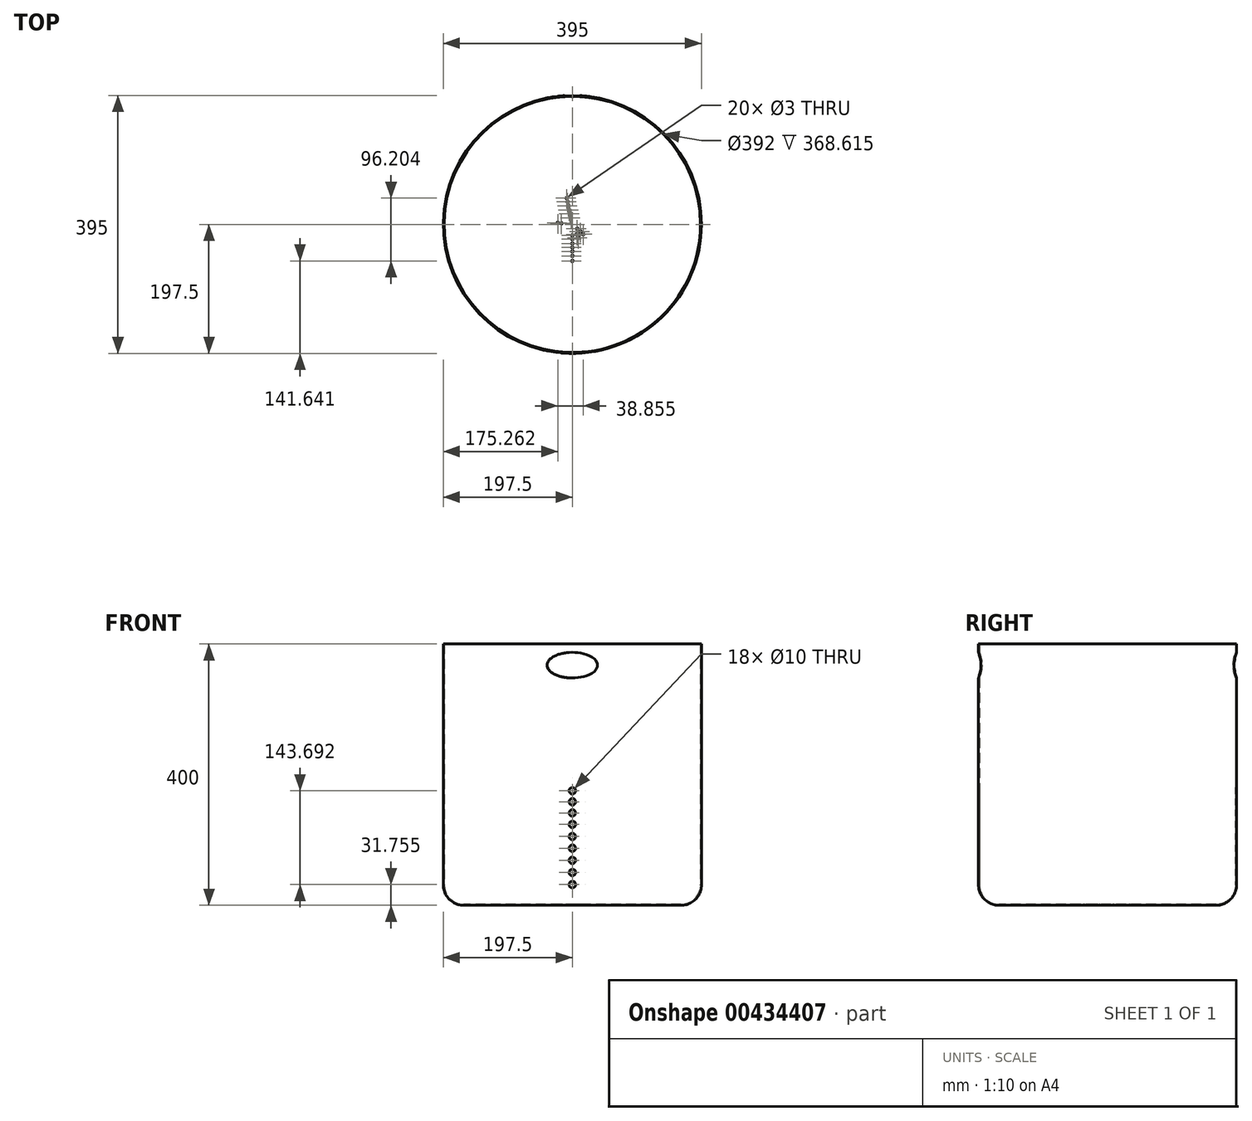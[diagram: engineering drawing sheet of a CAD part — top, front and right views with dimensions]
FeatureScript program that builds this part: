
annotation { "Feature Type Name" : "Feature", "Feature Type Description" : "" }
export const myFeature = defineFeature(function(context is Context, id is Id, definition is map)
    precondition{}
    {
        {
            var Q0;
            Q0=qCreatedBy(makeId("Top.planeOp"),FACE);
            var sketch = newSketch(context, id + "F0", { "sketchPlane" : qUnion([Q0])});
            skCircle(sketch, "E0", {"center": v(0, 0) * mm, "radius": 197.5 * mm});
            skSolve(sketch);
        }
        {
            var Q0;
            Q0 = qSketchRegion(id + "F0", true);
            extrude(context, id + "F1", {"entities" : qUnion([Q0]), "depth" : 400 * mm});
        }
        {
            var Q0;
            Q0=makeQuery(id+"F1.opExtrude","CAP_EDGE",EDGE,{"disambiguationData":[OSD([sQuery(id+"F0.wireOp",EDGE,"E0")])],"isStart":true});
            fillet(context, id + "F2", {"entities" : qUnion([Q0]), "radius" : 31.38 * mm, "tangentPropagation" : true, "allowEdgeOverflow" : false});
        }
        {
            var Q0;
            Q0=makeQuery(id+"F1.opExtrude","CAP_FACE",FACE,{"disambiguationData":[OSD([sQuery(id+"F0.wireOp",EDGE,"E0")])],"isStart":false});
            shell(context, id + "F3", {"entities" : qUnion([Q0]), "thickness" : 1.5 * mm});
        }
        {
            var Q0;
            Q0=makeQuery(id+"F1.opExtrude","CAP_FACE",FACE,{"disambiguationData":[OSD([sQuery(id+"F0.wireOp",EDGE,"E0")])],"isStart":true});
            var sketch = newSketch(context, id + "F4", { "sketchPlane" : qUnion([Q0])});
            skCircle(sketch, "E1", {"center": v(0, 3.82) * mm, "radius": 1.5 * mm});
            skCircle(sketch, "E2", {"center": v(0, 9.97) * mm, "radius": 1.5 * mm});
            skCircle(sketch, "E3", {"center": v(0, 16.8) * mm, "radius": 1.5 * mm});
            skCircle(sketch, "E4", {"center": v(0, 22.36) * mm, "radius": 1.5 * mm});
            skCircle(sketch, "E5", {"center": v(0, 29.28) * mm, "radius": 1.5 * mm});
            skCircle(sketch, "E6", {"center": v(0, 35.35) * mm, "radius": 1.5 * mm});
            skCircle(sketch, "E7", {"center": v(0, 41.25) * mm, "radius": 1.5 * mm});
            skCircle(sketch, "E8", {"center": v(0, 48.17) * mm, "radius": 1.5 * mm});
            skCircle(sketch, "E9", {"center": v(0, 55.86) * mm, "radius": 1.5 * mm});
            skCircle(sketch, "E10.1.0", {"center": v(-53.13, 17.26) * mm, "radius": 1.5 * mm});
            skCircle(sketch, "E10.1.1", {"center": v(-3.63, 1.18) * mm, "radius": 1.5 * mm});
            skCircle(sketch, "E10.1.2", {"center": v(-9.48, 3.08) * mm, "radius": 1.5 * mm});
            skCircle(sketch, "E10.1.3", {"center": v(-39.23, 12.75) * mm, "radius": 1.5 * mm});
            skCircle(sketch, "E10.1.4", {"center": v(-33.62, 10.92) * mm, "radius": 1.5 * mm});
            skCircle(sketch, "E10.1.5", {"center": v(-21.27, 6.9) * mm, "radius": 1.5 * mm});
            skCircle(sketch, "E10.1.6", {"center": v(-27.85, 9.05) * mm, "radius": 1.5 * mm});
            skCircle(sketch, "E10.1.7", {"center": v(-45.81, 14.88) * mm, "radius": 1.5 * mm});
            skCircle(sketch, "E10.1.8", {"center": v(-15.98, 5.2) * mm, "radius": 1.5 * mm});
            skCircle(sketch, "E10.2.0", {"center": v(-32.83, -45.2) * mm, "radius": 1.5 * mm});
            skCircle(sketch, "E10.2.1", {"center": v(-2.24, -3.09) * mm, "radius": 1.5 * mm});
            skCircle(sketch, "E10.2.2", {"center": v(-5.86, -8.07) * mm, "radius": 1.5 * mm});
            skCircle(sketch, "E10.2.3", {"center": v(-24.24, -33.37) * mm, "radius": 1.5 * mm});
            skCircle(sketch, "E10.2.4", {"center": v(-20.78, -28.6) * mm, "radius": 1.5 * mm});
            skCircle(sketch, "E10.2.5", {"center": v(-13.14, -18.1) * mm, "radius": 1.5 * mm});
            skCircle(sketch, "E10.2.6", {"center": v(-17.21, -23.7) * mm, "radius": 1.5 * mm});
            skCircle(sketch, "E10.2.7", {"center": v(-28.31, -38.97) * mm, "radius": 1.5 * mm});
            skCircle(sketch, "E10.2.8", {"center": v(-9.88, -13.6) * mm, "radius": 1.5 * mm});
            skCircle(sketch, "E10.3.0", {"center": v(32.83, -45.2) * mm, "radius": 1.5 * mm});
            skCircle(sketch, "E10.3.1", {"center": v(2.24, -3.09) * mm, "radius": 1.5 * mm});
            skCircle(sketch, "E10.3.2", {"center": v(5.86, -8.07) * mm, "radius": 1.5 * mm});
            skCircle(sketch, "E10.3.3", {"center": v(24.24, -33.37) * mm, "radius": 1.5 * mm});
            skCircle(sketch, "E10.3.4", {"center": v(20.78, -28.6) * mm, "radius": 1.5 * mm});
            skCircle(sketch, "E10.3.5", {"center": v(13.14, -18.1) * mm, "radius": 1.5 * mm});
            skCircle(sketch, "E10.3.6", {"center": v(17.21, -23.7) * mm, "radius": 1.5 * mm});
            skCircle(sketch, "E10.3.7", {"center": v(28.31, -38.97) * mm, "radius": 1.5 * mm});
            skCircle(sketch, "E10.3.8", {"center": v(9.88, -13.6) * mm, "radius": 1.5 * mm});
            skCircle(sketch, "E10.4.0", {"center": v(53.13, 17.26) * mm, "radius": 1.5 * mm});
            skCircle(sketch, "E10.4.1", {"center": v(3.63, 1.18) * mm, "radius": 1.5 * mm});
            skCircle(sketch, "E10.4.2", {"center": v(9.48, 3.08) * mm, "radius": 1.5 * mm});
            skCircle(sketch, "E10.4.3", {"center": v(39.23, 12.75) * mm, "radius": 1.5 * mm});
            skCircle(sketch, "E10.4.4", {"center": v(33.62, 10.92) * mm, "radius": 1.5 * mm});
            skCircle(sketch, "E10.4.5", {"center": v(21.27, 6.9) * mm, "radius": 1.5 * mm});
            skCircle(sketch, "E10.4.6", {"center": v(27.85, 9.05) * mm, "radius": 1.5 * mm});
            skCircle(sketch, "E10.4.7", {"center": v(45.81, 14.88) * mm, "radius": 1.5 * mm});
            skCircle(sketch, "E10.4.8", {"center": v(15.98, 5.2) * mm, "radius": 1.5 * mm});
            skPoint(sketch, "E10.center", {"position": v(0, 0) * mm});
            skCircle(sketch, "E11.1.0", {"center": v(-7.4, 6.67) * mm, "radius": 1.5 * mm});
            skCircle(sketch, "E11.1.1", {"center": v(-26.27, 23.65) * mm, "radius": 1.5 * mm});
            skCircle(sketch, "E11.1.2", {"center": v(-16.62, 14.96) * mm, "radius": 1.5 * mm});
            skCircle(sketch, "E11.1.3", {"center": v(-12.49, 11.25) * mm, "radius": 1.5 * mm});
            skCircle(sketch, "E11.1.4", {"center": v(-21.76, 19.6) * mm, "radius": 1.5 * mm});
            skCircle(sketch, "E11.1.5", {"center": v(6.84, 15.35) * mm, "radius": 1.5 * mm});
            skCircle(sketch, "E11.1.6", {"center": v(-35.8, 32.23) * mm, "radius": 1.5 * mm});
            skCircle(sketch, "E11.1.7", {"center": v(-30.65, 27.6) * mm, "radius": 1.5 * mm});
            skCircle(sketch, "E11.1.8", {"center": v(-41.51, 37.38) * mm, "radius": 1.5 * mm});
            skCircle(sketch, "E11.1.9", {"center": v(7.35, -34.58) * mm, "radius": 1.5 * mm});
            skCircle(sketch, "E11.1.10", {"center": v(6.09, -28.64) * mm, "radius": 1.5 * mm});
            skCircle(sketch, "E11.1.11", {"center": v(-8.63, -4.98) * mm, "radius": 1.5 * mm});
            skCircle(sketch, "E11.1.12", {"center": v(-14.55, -8.4) * mm, "radius": 1.5 * mm});
            skCircle(sketch, "E11.1.13", {"center": v(-19.36, -11.18) * mm, "radius": 1.5 * mm});
            skCircle(sketch, "E11.1.14", {"center": v(-25.36, -14.64) * mm, "radius": 1.5 * mm});
            skCircle(sketch, "E11.1.15", {"center": v(-30.61, -17.67) * mm, "radius": 1.5 * mm});
            skCircle(sketch, "E11.1.16", {"center": v(-35.72, -20.62) * mm, "radius": 1.5 * mm});
            skCircle(sketch, "E11.1.17", {"center": v(-41.71, -24.08) * mm, "radius": 1.5 * mm});
            skCircle(sketch, "E11.1.18", {"center": v(-48.38, -27.93) * mm, "radius": 1.5 * mm});
            skCircle(sketch, "E11.1.19", {"center": v(29.12, -3.06) * mm, "radius": 1.5 * mm});
            skCircle(sketch, "E11.1.20", {"center": v(35.16, -3.7) * mm, "radius": 1.5 * mm});
            skCircle(sketch, "E11.1.21", {"center": v(3.5, -16.44) * mm, "radius": 1.5 * mm});
            skCircle(sketch, "E11.1.22", {"center": v(4.65, -21.87) * mm, "radius": 1.5 * mm});
            skCircle(sketch, "E11.1.23", {"center": v(11.61, -54.64) * mm, "radius": 1.5 * mm});
            skCircle(sketch, "E11.1.24", {"center": v(8.58, -40.34) * mm, "radius": 1.5 * mm});
            skCircle(sketch, "E11.1.25", {"center": v(10.01, -47.12) * mm, "radius": 1.5 * mm});
            skCircle(sketch, "E11.1.26", {"center": v(22.24, -2.34) * mm, "radius": 1.5 * mm});
            skCircle(sketch, "E11.1.27", {"center": v(2.07, -9.75) * mm, "radius": 1.5 * mm});
            skCircle(sketch, "E11.1.28", {"center": v(55.55, -5.84) * mm, "radius": 1.5 * mm});
            skCircle(sketch, "E11.1.29", {"center": v(16.71, -1.76) * mm, "radius": 1.5 * mm});
            skCircle(sketch, "E11.1.30", {"center": v(41.02, -4.31) * mm, "radius": 1.5 * mm});
            skCircle(sketch, "E11.1.31", {"center": v(47.9, -5.03) * mm, "radius": 1.5 * mm});
            skCircle(sketch, "E11.1.32", {"center": v(9.1, 20.43) * mm, "radius": 1.5 * mm});
            skCircle(sketch, "E11.1.33", {"center": v(11.91, 26.75) * mm, "radius": 1.5 * mm});
            skCircle(sketch, "E11.1.34", {"center": v(14.38, 32.3) * mm, "radius": 1.5 * mm});
            skCircle(sketch, "E11.1.35", {"center": v(16.78, 37.68) * mm, "radius": 1.5 * mm});
            skCircle(sketch, "E11.1.36", {"center": v(19.6, 44) * mm, "radius": 1.5 * mm});
            skCircle(sketch, "E11.1.37", {"center": v(22.72, 51.03) * mm, "radius": 1.5 * mm});
            skCircle(sketch, "E11.2.0", {"center": v(-2.07, -9.75) * mm, "radius": 1.5 * mm});
            skCircle(sketch, "E11.2.1", {"center": v(-7.35, -34.58) * mm, "radius": 1.5 * mm});
            skCircle(sketch, "E11.2.2", {"center": v(-4.65, -21.87) * mm, "radius": 1.5 * mm});
            skCircle(sketch, "E11.2.3", {"center": v(-3.5, -16.44) * mm, "radius": 1.5 * mm});
            skCircle(sketch, "E11.2.4", {"center": v(-6.09, -28.64) * mm, "radius": 1.5 * mm});
            skCircle(sketch, "E11.2.5", {"center": v(-16.71, -1.76) * mm, "radius": 1.5 * mm});
            skCircle(sketch, "E11.2.6", {"center": v(-10.01, -47.12) * mm, "radius": 1.5 * mm});
            skCircle(sketch, "E11.2.7", {"center": v(-8.58, -40.34) * mm, "radius": 1.5 * mm});
            skCircle(sketch, "E11.2.8", {"center": v(-11.61, -54.64) * mm, "radius": 1.5 * mm});
            skCircle(sketch, "E11.2.9", {"center": v(26.27, 23.65) * mm, "radius": 1.5 * mm});
            skCircle(sketch, "E11.2.10", {"center": v(21.76, 19.6) * mm, "radius": 1.5 * mm});
            skCircle(sketch, "E11.2.11", {"center": v(8.63, -4.98) * mm, "radius": 1.5 * mm});
            skCircle(sketch, "E11.2.12", {"center": v(14.55, -8.4) * mm, "radius": 1.5 * mm});
            skCircle(sketch, "E11.2.13", {"center": v(19.36, -11.18) * mm, "radius": 1.5 * mm});
            skCircle(sketch, "E11.2.14", {"center": v(25.36, -14.64) * mm, "radius": 1.5 * mm});
            skCircle(sketch, "E11.2.15", {"center": v(30.61, -17.67) * mm, "radius": 1.5 * mm});
            skCircle(sketch, "E11.2.16", {"center": v(35.72, -20.62) * mm, "radius": 1.5 * mm});
            skCircle(sketch, "E11.2.17", {"center": v(41.71, -24.08) * mm, "radius": 1.5 * mm});
            skCircle(sketch, "E11.2.18", {"center": v(48.38, -27.93) * mm, "radius": 1.5 * mm});
            skCircle(sketch, "E11.2.19", {"center": v(-11.91, 26.75) * mm, "radius": 1.5 * mm});
            skCircle(sketch, "E11.2.20", {"center": v(-14.38, 32.3) * mm, "radius": 1.5 * mm});
            skCircle(sketch, "E11.2.21", {"center": v(12.49, 11.25) * mm, "radius": 1.5 * mm});
            skCircle(sketch, "E11.2.22", {"center": v(16.62, 14.96) * mm, "radius": 1.5 * mm});
            skCircle(sketch, "E11.2.23", {"center": v(41.51, 37.38) * mm, "radius": 1.5 * mm});
            skCircle(sketch, "E11.2.24", {"center": v(30.65, 27.6) * mm, "radius": 1.5 * mm});
            skCircle(sketch, "E11.2.25", {"center": v(35.8, 32.23) * mm, "radius": 1.5 * mm});
            skCircle(sketch, "E11.2.26", {"center": v(-9.1, 20.43) * mm, "radius": 1.5 * mm});
            skCircle(sketch, "E11.2.27", {"center": v(7.4, 6.67) * mm, "radius": 1.5 * mm});
            skCircle(sketch, "E11.2.28", {"center": v(-22.72, 51.03) * mm, "radius": 1.5 * mm});
            skCircle(sketch, "E11.2.29", {"center": v(-6.84, 15.35) * mm, "radius": 1.5 * mm});
            skCircle(sketch, "E11.2.30", {"center": v(-16.78, 37.68) * mm, "radius": 1.5 * mm});
            skCircle(sketch, "E11.2.31", {"center": v(-19.6, 44) * mm, "radius": 1.5 * mm});
            skCircle(sketch, "E11.2.32", {"center": v(-22.24, -2.34) * mm, "radius": 1.5 * mm});
            skCircle(sketch, "E11.2.33", {"center": v(-29.12, -3.06) * mm, "radius": 1.5 * mm});
            skCircle(sketch, "E11.2.34", {"center": v(-35.16, -3.7) * mm, "radius": 1.5 * mm});
            skCircle(sketch, "E11.2.35", {"center": v(-41.02, -4.31) * mm, "radius": 1.5 * mm});
            skCircle(sketch, "E11.2.36", {"center": v(-47.9, -5.03) * mm, "radius": 1.5 * mm});
            skCircle(sketch, "E11.2.37", {"center": v(-55.55, -5.84) * mm, "radius": 1.5 * mm});
            skSolve(sketch);
        }
        {
            var Q0;
            Q0=makeQuery(id+"F4.imprint","IMPRINT",FACE,{"disambiguationData":[TD([[makeQuery(id+"F4.imprint","IMPRINT",EDGE,{"derivedFrom":sQuery(id+"F4.wireOp",EDGE,"E9")}),1.0]])]});
            var Q1;
            Q1=makeQuery(id+"F4.imprint","IMPRINT",FACE,{"disambiguationData":[TD([[makeQuery(id+"F4.imprint","IMPRINT",EDGE,{"derivedFrom":sQuery(id+"F4.wireOp",EDGE,"E8")}),1.0]])]});
            var Q2;
            Q2=makeQuery(id+"F4.imprint","IMPRINT",FACE,{"disambiguationData":[TD([[makeQuery(id+"F4.imprint","IMPRINT",EDGE,{"derivedFrom":sQuery(id+"F4.wireOp",EDGE,"E7")}),1.0]])]});
            var Q3;
            Q3=makeQuery(id+"F4.imprint","IMPRINT",FACE,{"disambiguationData":[TD([[makeQuery(id+"F4.imprint","IMPRINT",EDGE,{"derivedFrom":sQuery(id+"F4.wireOp",EDGE,"E6")}),1.0]])]});
            var Q4;
            Q4=makeQuery(id+"F4.imprint","IMPRINT",FACE,{"disambiguationData":[TD([[makeQuery(id+"F4.imprint","IMPRINT",EDGE,{"derivedFrom":sQuery(id+"F4.wireOp",EDGE,"E5")}),1.0]])]});
            var Q5;
            Q5=makeQuery(id+"F4.imprint","IMPRINT",FACE,{"disambiguationData":[TD([[makeQuery(id+"F4.imprint","IMPRINT",EDGE,{"derivedFrom":sQuery(id+"F4.wireOp",EDGE,"E4")}),1.0]])]});
            var Q6;
            Q6=makeQuery(id+"F4.imprint","IMPRINT",FACE,{"disambiguationData":[TD([[makeQuery(id+"F4.imprint","IMPRINT",EDGE,{"derivedFrom":sQuery(id+"F4.wireOp",EDGE,"E3")}),1.0]])]});
            var Q7;
            Q7=makeQuery(id+"F4.imprint","IMPRINT",FACE,{"disambiguationData":[TD([[makeQuery(id+"F4.imprint","IMPRINT",EDGE,{"derivedFrom":sQuery(id+"F4.wireOp",EDGE,"E11.1.5")}),1.0]])]});
            var Q8;
            Q8=makeQuery(id+"F4.imprint","IMPRINT",FACE,{"disambiguationData":[TD([[makeQuery(id+"F4.imprint","IMPRINT",EDGE,{"derivedFrom":sQuery(id+"F4.wireOp",EDGE,"E11.1.32")}),1.0]])]});
            var Q9;
            Q9=makeQuery(id+"F4.imprint","IMPRINT",FACE,{"disambiguationData":[TD([[makeQuery(id+"F4.imprint","IMPRINT",EDGE,{"derivedFrom":sQuery(id+"F4.wireOp",EDGE,"E11.2.22")}),1.0]])]});
            var Q10;
            Q10=makeQuery(id+"F4.imprint","IMPRINT",FACE,{"disambiguationData":[TD([[makeQuery(id+"F4.imprint","IMPRINT",EDGE,{"derivedFrom":sQuery(id+"F4.wireOp",EDGE,"E11.2.21")}),1.0]])]});
            var Q11;
            Q11=makeQuery(id+"F4.imprint","IMPRINT",FACE,{"disambiguationData":[TD([[makeQuery(id+"F4.imprint","IMPRINT",EDGE,{"derivedFrom":sQuery(id+"F4.wireOp",EDGE,"E11.2.27")}),1.0]])]});
            var Q12;
            Q12=makeQuery(id+"F4.imprint","IMPRINT",FACE,{"disambiguationData":[TD([[makeQuery(id+"F4.imprint","IMPRINT",EDGE,{"derivedFrom":sQuery(id+"F4.wireOp",EDGE,"E11.2.0")}),1.0]])]});
            var Q13;
            Q13=makeQuery(id+"F4.imprint","IMPRINT",FACE,{"disambiguationData":[TD([[makeQuery(id+"F4.imprint","IMPRINT",EDGE,{"derivedFrom":sQuery(id+"F4.wireOp",EDGE,"E11.2.3")}),1.0]])]});
            var Q14;
            Q14=makeQuery(id+"F4.imprint","IMPRINT",FACE,{"disambiguationData":[TD([[makeQuery(id+"F4.imprint","IMPRINT",EDGE,{"derivedFrom":sQuery(id+"F4.wireOp",EDGE,"E11.2.2")}),1.0]])]});
            var Q15;
            Q15=makeQuery(id+"F4.imprint","IMPRINT",FACE,{"disambiguationData":[TD([[makeQuery(id+"F4.imprint","IMPRINT",EDGE,{"derivedFrom":sQuery(id+"F4.wireOp",EDGE,"E11.2.4")}),1.0]])]});
            var Q16;
            Q16=makeQuery(id+"F4.imprint","IMPRINT",FACE,{"disambiguationData":[TD([[makeQuery(id+"F4.imprint","IMPRINT",EDGE,{"derivedFrom":sQuery(id+"F4.wireOp",EDGE,"E11.2.1")}),1.0]])]});
            var Q17;
            Q17=makeQuery(id+"F4.imprint","IMPRINT",FACE,{"disambiguationData":[TD([[makeQuery(id+"F4.imprint","IMPRINT",EDGE,{"derivedFrom":sQuery(id+"F4.wireOp",EDGE,"E11.2.7")}),1.0]])]});
            var Q18;
            Q18=makeQuery(id+"F4.imprint","IMPRINT",FACE,{"disambiguationData":[TD([[makeQuery(id+"F4.imprint","IMPRINT",EDGE,{"derivedFrom":sQuery(id+"F4.wireOp",EDGE,"E11.2.5")}),1.0]])]});
            var Q19;
            Q19=makeQuery(id+"F4.imprint","IMPRINT",FACE,{"disambiguationData":[TD([[makeQuery(id+"F4.imprint","IMPRINT",EDGE,{"derivedFrom":sQuery(id+"F4.wireOp",EDGE,"E11.2.32")}),1.0]])]});
            extrude(context, id + "F5", {"entities" : qUnion([Q0, Q1, Q2, Q3, Q4, Q5, Q6, Q7, Q8, Q9, Q10, Q11, Q12, Q13, Q14, Q15, Q16, Q17, Q18, Q19]), "operationType" : NewBodyOperationType.REMOVE, "oppositeDirection" : true, "depth" : 25 * mm});
        }
        {
            var Q0;
            Q0=qCreatedBy(makeId("Front.planeOp"),FACE);
            var sketch = newSketch(context, id + "F6", { "sketchPlane" : qUnion([Q0])});
            skEllipse(sketch, "E12", {"center": v(0, 367.68) * mm, "majorRadius": 38.72 * mm, "minorRadius": 19.6 * mm, "majorAxis": v(-1, 0)});
            skSolve(sketch);
        }
        {
            var Q0;
            Q0=makeQuery(id+"F6.imprint","IMPRINT",FACE,{"disambiguationData":[TD([[makeQuery(id+"F6.imprint","IMPRINT",EDGE,{"derivedFrom":sQuery(id+"F6.wireOp",EDGE,"E12")}),1.0]])]});
            var Q1;
            Q1=sQuery(id+"F6.wireOp",EDGE,"E12");
            extrude(context, id + "F7", {"entities" : qUnion([Q0]), "operationType" : NewBodyOperationType.REMOVE, "surfaceEntities" : qUnion([Q1]), "endBound" : BoundingType.SYMMETRIC, "depth" : 10000 * mm});
        }
        {
            var Q0;
            Q0=qCreatedBy(makeId("Front.planeOp"),FACE);
            var sketch = newSketch(context, id + "F8", { "sketchPlane" : qUnion([Q0])});
            skCircle(sketch, "E13", {"center": v(0, 31.76) * mm, "radius": 5 * mm});
            skCircle(sketch, "E14", {"center": v(0, 50.3) * mm, "radius": 5 * mm});
            skCircle(sketch, "E15", {"center": v(0, 68.84) * mm, "radius": 5 * mm});
            skCircle(sketch, "E16", {"center": v(0, 87.38) * mm, "radius": 5 * mm});
            skCircle(sketch, "E17", {"center": v(0, 105.4) * mm, "radius": 5 * mm});
            skCircle(sketch, "E18", {"center": v(0, 123.94) * mm, "radius": 5 * mm});
            skCircle(sketch, "E19", {"center": v(0, 141.46) * mm, "radius": 5 * mm});
            skCircle(sketch, "E20", {"center": v(0, 158.45) * mm, "radius": 5 * mm});
            skCircle(sketch, "E21", {"center": v(0, 175.45) * mm, "radius": 5 * mm});
            skSolve(sketch);
        }
        {
            var Q0;
            Q0 = qSketchRegion(id + "F8", true);
            extrude(context, id + "F9", {"entities" : qUnion([Q0]), "operationType" : NewBodyOperationType.REMOVE, "endBound" : BoundingType.SYMMETRIC, "oppositeDirection" : true, "depth" : 1000 * mm});
        }
    });
